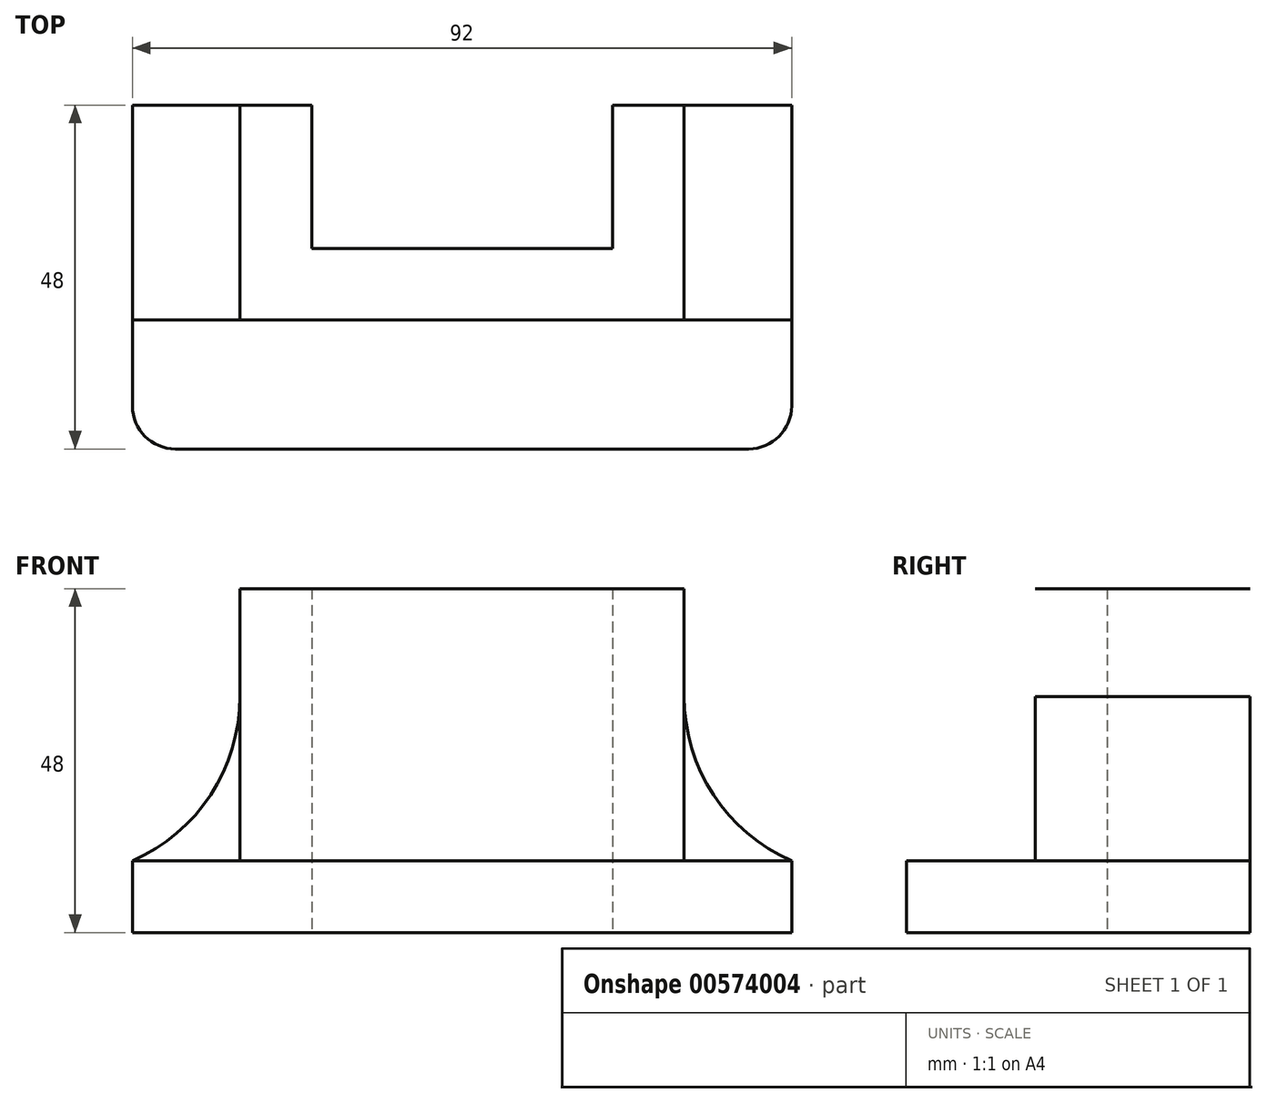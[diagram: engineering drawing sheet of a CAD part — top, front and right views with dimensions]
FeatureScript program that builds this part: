
annotation { "Feature Type Name" : "Feature", "Feature Type Description" : "" }
export const myFeature = defineFeature(function(context is Context, id is Id, definition is map)
    precondition{}
    {
        {
            var Q0;
            Q0=qCreatedBy(makeId("Top.planeOp"),FACE);
            var sketch = newSketch(context, id + "F0", { "sketchPlane" : qUnion([Q0])});
            skLineSegment(sketch, "E0", {"start": v(46, 30) * mm, "end": v(46, -12) * mm});
            skLineSegment(sketch, "E1", {"start": v(40, -18) * mm, "end": v(-40, -18) * mm});
            skLineSegment(sketch, "E2", {"start": v(-46, -12) * mm, "end": v(-46, 30) * mm});
            skLineSegment(sketch, "E3", {"start": v(-46, 30) * mm, "end": v(-31, 30) * mm});
            skLineSegment(sketch, "E4", {"start": v(-31, 30) * mm, "end": v(-31, 0) * mm});
            skLineSegment(sketch, "E5", {"start": v(-31, 0) * mm, "end": v(31, 0) * mm});
            skLineSegment(sketch, "E6", {"start": v(31, 0) * mm, "end": v(31, 30) * mm});
            skLineSegment(sketch, "E7", {"start": v(31, 30) * mm, "end": v(46, 30) * mm});
            skPoint(sketch, "E8.visualSharp", {"position": v(-46, -18) * mm});
            skArc(sketch, "E8.filletArc", {"start": v(-46, -12) * mm, "mid": v(-44.24, -16.24) * mm, "end": v(-40, -18) * mm});
            skPoint(sketch, "E9.visualSharp", {"position": v(46, -18) * mm});
            skArc(sketch, "E9.filletArc", {"start": v(40, -18) * mm, "mid": v(44.24, -16.24) * mm, "end": v(46, -12) * mm});
            skSolve(sketch);
        }
        {
            var Q0;
            Q0=qCreatedBy(makeId("Top.planeOp"),FACE);
            var sketch = newSketch(context, id + "F1", { "sketchPlane" : qUnion([Q0])});
            skLineSegment(sketch, "E10", {"start": v(-31, 30) * mm, "end": v(-21, 30) * mm});
            skLineSegment(sketch, "E11", {"start": v(-21, 30) * mm, "end": v(-21, 10) * mm});
            skLineSegment(sketch, "E12", {"start": v(-21, 10) * mm, "end": v(21, 10) * mm});
            skLineSegment(sketch, "E13", {"start": v(21, 10) * mm, "end": v(21, 30) * mm});
            skLineSegment(sketch, "E14", {"start": v(21, 30) * mm, "end": v(31, 30) * mm});
            skLineSegment(sketch, "E15", {"start": v(-31, 30) * mm, "end": v(-31, 0) * mm});
            skLineSegment(sketch, "E16", {"start": v(-31, 0) * mm, "end": v(31, 0) * mm});
            skLineSegment(sketch, "E17", {"start": v(31, 0) * mm, "end": v(31, 30) * mm});
            skSolve(sketch);
        }
        {
            var Q0;
            Q0 = qSketchRegion(id + "F1", true);
            extrude(context, id + "F2", {"entities" : qUnion([Q0]), "depth" : 48 * mm, "offsetDistance" : 25 * mm});
        }
        {
            var Q0;
            Q0 = qSketchRegion(id + "F0", true);
            extrude(context, id + "F3", {"entities" : qUnion([Q0]), "operationType" : NewBodyOperationType.ADD, "depth" : 10 * mm, "offsetDistance" : 25 * mm});
        }
        {
            var Q0;
            Q0=qCreatedBy(makeId("Front.planeOp"),FACE);
            var sketch = newSketch(context, id + "F4", { "sketchPlane" : qUnion([Q0])});
            skArc(sketch, "E18", {"start": v(-46, 10) * mm, "mid": v(-35.08, 19.22) * mm, "end": v(-31, 32.91) * mm});
            skArc(sketch, "E19", {"start": v(31, 32.91) * mm, "mid": v(35.08, 19.22) * mm, "end": v(46, 10) * mm});
            skLineSegment(sketch, "E20", {"start": v(-31, 32.91) * mm, "end": v(-31, 10) * mm});
            skLineSegment(sketch, "E21", {"start": v(-31, 10) * mm, "end": v(-46, 10) * mm});
            skLineSegment(sketch, "E22", {"start": v(31, 32.91) * mm, "end": v(31, 10) * mm});
            skLineSegment(sketch, "E23", {"start": v(31, 10) * mm, "end": v(46, 10) * mm});
            skSolve(sketch);
        }
        {
            var Q0;
            Q0 = qSketchRegion(id + "F4", true);
            extrude(context, id + "F5", {"entities" : qUnion([Q0]), "depth" : -30 * mm, "offsetDistance" : 25 * mm});
        }
    });
